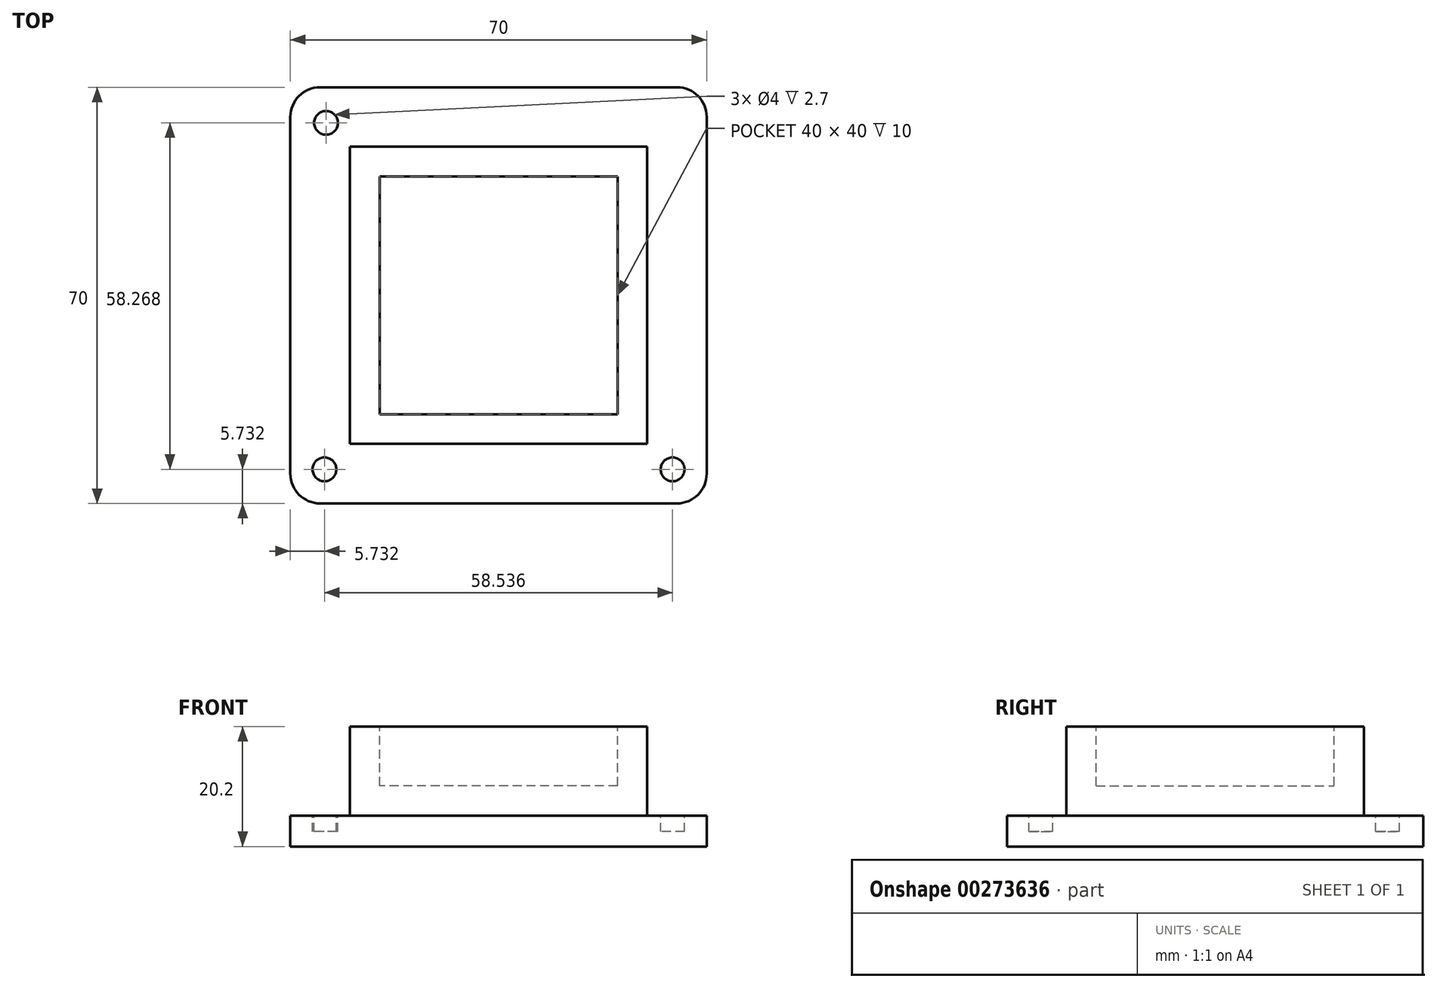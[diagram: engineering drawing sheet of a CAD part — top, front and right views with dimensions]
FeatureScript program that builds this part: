
annotation { "Feature Type Name" : "Feature", "Feature Type Description" : "" }
export const myFeature = defineFeature(function(context is Context, id is Id, definition is map)
    precondition{}
    {
        {
            var Q0;
            Q0=qCreatedBy(makeId("Top.planeOp"),FACE);
            var sketch = newSketch(context, id + "F0", { "sketchPlane" : qUnion([Q0])});
            skLineSegment(sketch, "E0.bottom", {"start": v(35, -35) * mm, "end": v(-35, -35) * mm});
            skLineSegment(sketch, "E0.top", {"start": v(35, 35) * mm, "end": v(-35, 35) * mm});
            skLineSegment(sketch, "E0.left", {"start": v(35, -35) * mm, "end": v(35, 35) * mm});
            skLineSegment(sketch, "E0.right", {"start": v(-35, -35) * mm, "end": v(-35, 35) * mm});
            skPoint(sketch, "E0.middle", {"position": v(0, 0) * mm});
            skSolve(sketch);
        }
        {
            var Q0;
            Q0=makeQuery(id+"F0.imprint","IMPRINT",FACE,{"disambiguationData":[TD([[makeQuery(id+"F0.imprint","IMPRINT",EDGE,{"derivedFrom":sQuery(id+"F0.wireOp",EDGE,"E0.bottom")}),-1.0]])]});
            extrude(context, id + "F1", {"entities" : qUnion([Q0]), "depth" : 5.2 * mm});
        }
        {
            var Q0;
            Q0=makeQuery(id+"F1.opExtrude","CAP_FACE",FACE,{"disambiguationData":[OSD([sQuery(id+"F0.wireOp",EDGE,"E0.bottom"),sQuery(id+"F0.wireOp",EDGE,"E0.top"),sQuery(id+"F0.wireOp",EDGE,"E0.left"),sQuery(id+"F0.wireOp",EDGE,"E0.right")])],"isStart":false});
            var sketch = newSketch(context, id + "F2", { "sketchPlane" : qUnion([Q0])});
            skLineSegment(sketch, "E1.bottom", {"start": v(25, -25) * mm, "end": v(-25, -25) * mm});
            skLineSegment(sketch, "E1.top", {"start": v(25, 25) * mm, "end": v(-25, 25) * mm});
            skLineSegment(sketch, "E1.left", {"start": v(25, -25) * mm, "end": v(25, 25) * mm});
            skLineSegment(sketch, "E1.right", {"start": v(-25, -25) * mm, "end": v(-25, 25) * mm});
            skPoint(sketch, "E1.middle", {"position": v(0, 0) * mm});
            skSolve(sketch);
        }
        {
            var Q0;
            Q0=makeQuery(id+"F2.imprint","IMPRINT",FACE,{"disambiguationData":[TD([[makeQuery(id+"F2.imprint","IMPRINT",EDGE,{"derivedFrom":sQuery(id+"F2.wireOp",EDGE,"E1.bottom")}),-1.0]])]});
            extrude(context, id + "F3", {"entities" : qUnion([Q0]), "operationType" : NewBodyOperationType.ADD, "depth" : 15 * mm});
        }
        {
            var Q0;
            Q0=makeQuery(id+"F1.opExtrude","SWEPT_EDGE",EDGE,{"disambiguationData":[OSD([sQuery(id+"F0.wireOp",EDGE,"E0.top"),sQuery(id+"F0.wireOp",EDGE,"E0.right")])]});
            var Q1;
            Q1=makeQuery(id+"F1.opExtrude","SWEPT_EDGE",EDGE,{"disambiguationData":[OSD([sQuery(id+"F0.wireOp",EDGE,"E0.top"),sQuery(id+"F0.wireOp",EDGE,"E0.left")])]});
            var Q2;
            Q2=makeQuery(id+"F1.opExtrude","SWEPT_EDGE",EDGE,{"disambiguationData":[OSD([sQuery(id+"F0.wireOp",EDGE,"E0.bottom"),sQuery(id+"F0.wireOp",EDGE,"E0.left")])]});
            var Q3;
            Q3=makeQuery(id+"F1.opExtrude","SWEPT_EDGE",EDGE,{"disambiguationData":[OSD([sQuery(id+"F0.wireOp",EDGE,"E0.bottom"),sQuery(id+"F0.wireOp",EDGE,"E0.right")])]});
            fillet(context, id + "F4", {"entities" : qUnion([Q0, Q1, Q2, Q3]), "radius" : 5 * mm, "tangentPropagation" : true, "allowEdgeOverflow" : false});
        }
        {
            var Q0;
            Q0=makeQuery(id+"F1.opExtrude","CAP_FACE",FACE,{"disambiguationData":[OSD([sQuery(id+"F0.wireOp",EDGE,"E0.bottom"),sQuery(id+"F0.wireOp",EDGE,"E0.top"),sQuery(id+"F0.wireOp",EDGE,"E0.left"),sQuery(id+"F0.wireOp",EDGE,"E0.right")])],"isStart":false});
            var sketch = newSketch(context, id + "F5", { "sketchPlane" : qUnion([Q0])});
            skLineSegment(sketch, "E2.0", {"start": v(-35, -30) * mm, "end": v(-35, 30) * mm, "construction": true});
            skPoint(sketch, "E3.0", {"position": v(-33.54, 33.54) * mm});
            skArc(sketch, "E4.0", {"start": v(-30, 35) * mm, "mid": v(-33.54, 33.54) * mm, "end": v(-35, 30) * mm});
            skLineSegment(sketch, "E5.0", {"start": v(30, 35) * mm, "end": v(-30, 35) * mm, "construction": true});
            skLineSegment(sketch, "E6.0", {"start": v(35, -30) * mm, "end": v(35, 30) * mm, "construction": true});
            skArc(sketch, "E7.0", {"start": v(30, -35) * mm, "mid": v(33.54, -33.54) * mm, "end": v(35, -30) * mm, "construction": true});
            skLineSegment(sketch, "E8.0", {"start": v(30, -35) * mm, "end": v(-30, -35) * mm, "construction": true});
            skArc(sketch, "E9.0", {"start": v(-35, -30) * mm, "mid": v(-33.54, -33.54) * mm, "end": v(-30, -35) * mm, "construction": true});
            skPoint(sketch, "E10.0", {"position": v(33.54, 33.54) * mm});
            skPoint(sketch, "E11", {"position": v(-33.54, -33.54) * mm});
            skPoint(sketch, "E12", {"position": v(33.54, -33.54) * mm});
            skLineSegment(sketch, "E13", {"start": v(25, -25) * mm, "end": v(33.54, -33.54) * mm, "construction": true});
            skLineSegment(sketch, "E14", {"start": v(-25, -25) * mm, "end": v(-33.54, -33.54) * mm, "construction": true});
            skPoint(sketch, "E15", {"position": v(-29, 29) * mm});
            skPoint(sketch, "E16", {"position": v(29.27, -29.27) * mm});
            skPoint(sketch, "E17", {"position": v(-29.27, -29.27) * mm});
            skCircle(sketch, "E18", {"center": v(-29, 29) * mm, "radius": 2 * mm});
            skCircle(sketch, "E19", {"center": v(29.27, -29.27) * mm, "radius": 2 * mm});
            skCircle(sketch, "E20", {"center": v(-29.27, -29.27) * mm, "radius": 2 * mm});
            skCircle(sketch, "E21.MirrorC", {"center": v(29, 29) * mm, "radius": 2 * mm});
            skSolve(sketch);
        }
        {
            var Q0;
            Q0=makeQuery(id+"F5.imprint","IMPRINT",FACE,{"disambiguationData":[TD([[makeQuery(id+"F5.imprint","IMPRINT",EDGE,{"derivedFrom":sQuery(id+"F5.wireOp",EDGE,"E18")}),1.0]])]});
            var Q1;
            Q1=makeQuery(id+"F5.imprint","IMPRINT",FACE,{"disambiguationData":[TD([[makeQuery(id+"F5.imprint","IMPRINT",EDGE,{"derivedFrom":sQuery(id+"F5.wireOp",EDGE,"RnxCyVwn-93m7-CxHI-HVAs-AC2wogrhx5ka")}),1.0]])]});
            var Q2;
            Q2=makeQuery(id+"F5.imprint","IMPRINT",FACE,{"disambiguationData":[TD([[makeQuery(id+"F5.imprint","IMPRINT",EDGE,{"derivedFrom":sQuery(id+"F5.wireOp",EDGE,"E19")}),1.0]])]});
            var Q3;
            Q3=makeQuery(id+"F5.imprint","IMPRINT",FACE,{"disambiguationData":[TD([[makeQuery(id+"F5.imprint","IMPRINT",EDGE,{"derivedFrom":sQuery(id+"F5.wireOp",EDGE,"E20")}),1.0]])]});
            extrude(context, id + "F6", {"entities" : qUnion([Q0, Q1, Q2, Q3]), "operationType" : NewBodyOperationType.REMOVE, "oppositeDirection" : true, "depth" : 2.7 * mm});
        }
        {
            var Q0;
            Q0=makeQuery(id+"F3.opExtrude","CAP_FACE",FACE,{"disambiguationData":[OSD([sQuery(id+"F2.wireOp",EDGE,"E1.bottom"),sQuery(id+"F2.wireOp",EDGE,"E1.top"),sQuery(id+"F2.wireOp",EDGE,"E1.left"),sQuery(id+"F2.wireOp",EDGE,"E1.right")])],"isStart":false});
            var sketch = newSketch(context, id + "F7", { "sketchPlane" : qUnion([Q0])});
            skSolve(sketch);
        }
        {
            var Q0;
            Q0=makeQuery(id+"F7.imprint","IMPRINT",FACE,{"disambiguationData":[TD([[makeQuery(id+"F7.imprint","IMPRINT",EDGE,{"derivedFrom":makeQuery(id+"F3.opExtrude","CAP_EDGE",EDGE,{"disambiguationData":[OSD([sQuery(id+"F2.wireOp",EDGE,"E1.bottom")])],"isStart":false})}),-1.0]])]});
            var sketch = newSketch(context, id + "F8", { "sketchPlane" : qUnion([Q0])});
            skLineSegment(sketch, "E22.bottom", {"start": v(20, -20) * mm, "end": v(-20, -20) * mm});
            skLineSegment(sketch, "E22.top", {"start": v(20, 20) * mm, "end": v(-20, 20) * mm});
            skLineSegment(sketch, "E22.left", {"start": v(20, -20) * mm, "end": v(20, 20) * mm});
            skLineSegment(sketch, "E22.right", {"start": v(-20, -20) * mm, "end": v(-20, 20) * mm});
            skSolve(sketch);
        }
        {
            var Q0;
            Q0=qSketchRegion(id+"F8",true);
            extrude(context, id + "F9", {"entities" : qUnion([Q0]), "operationType" : NewBodyOperationType.REMOVE, "oppositeDirection" : true, "depth" : 10 * mm});
        }
    });
